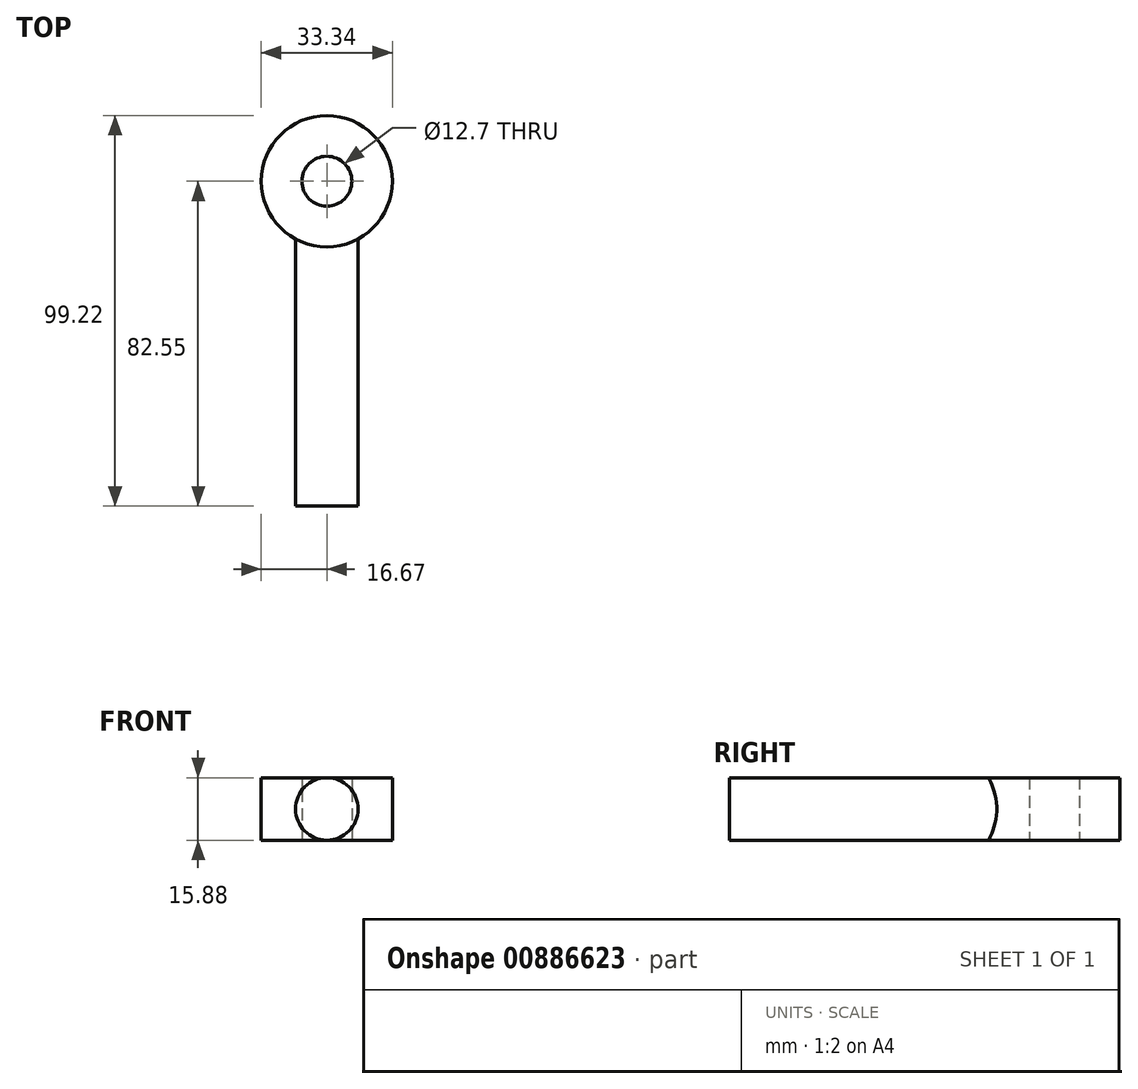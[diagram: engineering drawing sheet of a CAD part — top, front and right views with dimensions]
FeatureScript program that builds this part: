
annotation { "Feature Type Name" : "Feature", "Feature Type Description" : "" }
export const myFeature = defineFeature(function(context is Context, id is Id, definition is map)
    precondition{}
    {
        {
            assignVariable(context, id + "F0", {"name" : "RodEndA", "anyValue" : 12.7 * mm});
        }
        {
            assignVariable(context, id + "F1", {"name" : "RodEndC", "anyValue" : 15.88 * mm});
        }
        {
            assignVariable(context, id + "F2", {"name" : "RodEndE", "anyValue" : 63.5 * mm});
        }
        {
            var Q0;
            Q0=qCreatedBy(makeId("Top.planeOp"),FACE);
            var sketch = newSketch(context, id + "F3", { "sketchPlane" : qUnion([Q0])});
            skCircle(sketch, "E0", {"center": v(0, 0) * mm, "radius": 6.35 * mm});
            skCircle(sketch, "E1", {"center": v(0, 0) * mm, "radius": 16.67 * mm});
            skSolve(sketch);
        }
        {
            var Q0;
            Q0=makeQuery(id+"F3.imprint","IMPRINT",FACE,{"disambiguationData":[TD([[makeQuery(id+"F3.imprint","IMPRINT",EDGE,{"derivedFrom":sQuery(id+"F3.wireOp",EDGE,"E0")}),-1.0]])]});
            extrude(context, id + "F4", {"entities" : qUnion([Q0]), "endBound" : BoundingType.SYMMETRIC, "depth" : getVariable(context, 'RodEndC'), "offsetDistance" : 25.4 * mm});
        }
        {
            var Q0;
            Q0=qCreatedBy(makeId("Front.planeOp"),FACE);
            cPlane(context, id + "F5", {"entities" : qUnion([Q0]), "cplaneType" : CPlaneType.OFFSET, "offset" : getVariable(context, 'RodEndA') / 2, "width" : 152.4 * mm, "height" : 152.4 * mm});
        }
        {
            var Q0;
            Q0=qCreatedBy(id+"F5.planeOp",FACE);
            var sketch = newSketch(context, id + "F6", { "sketchPlane" : qUnion([Q0])});
            skCircle(sketch, "E2", {"center": v(0, 0) * mm, "radius": 7.94 * mm});
            skSolve(sketch);
        }
        {
            var Q0;
            Q0 = qSketchRegion(id + "F6", true);
            extrude(context, id + "F7", {"entities" : qUnion([Q0]), "operationType" : NewBodyOperationType.ADD, "depth" : getVariable(context, 'RodEndE') + getVariable(context, 'RodEndA'), "offsetDistance" : 25.4 * mm});
        }
    });
